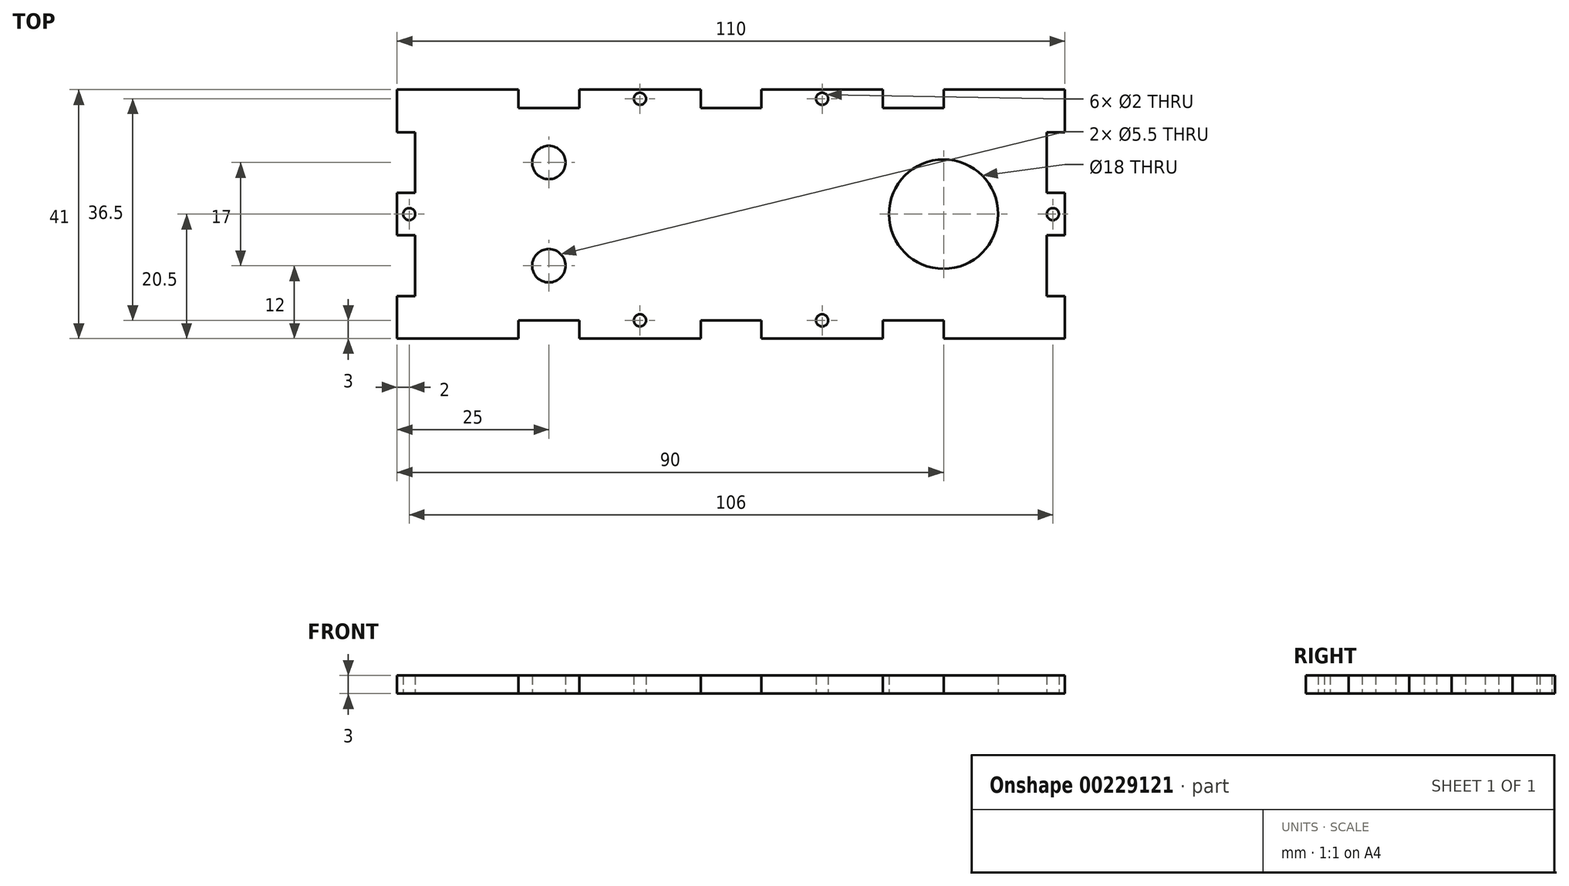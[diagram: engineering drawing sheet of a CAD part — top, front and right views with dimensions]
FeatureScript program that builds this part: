
annotation { "Feature Type Name" : "Feature", "Feature Type Description" : "" }
export const myFeature = defineFeature(function(context is Context, id is Id, definition is map)
    precondition{}
    {
        {
            var Q0;
            Q0=qCreatedBy(makeId("Top.planeOp"),FACE);
            var sketch = newSketch(context, id + "F0", { "sketchPlane" : qUnion([Q0])});
            skLineSegment(sketch, "E0", {"start": v(0, 0) * mm, "end": v(0, 7) * mm});
            skLineSegment(sketch, "E1", {"start": v(0, 7) * mm, "end": v(3, 7) * mm});
            skLineSegment(sketch, "E2", {"start": v(3, 7) * mm, "end": v(3, 17) * mm});
            skLineSegment(sketch, "E3", {"start": v(3, 17) * mm, "end": v(0, 17) * mm});
            skLineSegment(sketch, "E4", {"start": v(0, 17) * mm, "end": v(0, 24) * mm});
            skLineSegment(sketch, "E5", {"start": v(0, 24) * mm, "end": v(3, 24) * mm});
            skLineSegment(sketch, "E6", {"start": v(3, 24) * mm, "end": v(3, 34) * mm});
            skLineSegment(sketch, "E7", {"start": v(3, 34) * mm, "end": v(0, 34) * mm});
            skLineSegment(sketch, "E8", {"start": v(0, 34) * mm, "end": v(0, 41) * mm});
            skLineSegment(sketch, "E9", {"start": v(0, 0) * mm, "end": v(20, 0) * mm});
            skLineSegment(sketch, "E10", {"start": v(20, 0) * mm, "end": v(20, 3) * mm});
            skLineSegment(sketch, "E11", {"start": v(20, 3) * mm, "end": v(30, 3) * mm});
            skLineSegment(sketch, "E12", {"start": v(30, 3) * mm, "end": v(30, 0) * mm});
            skLineSegment(sketch, "E13", {"start": v(30, 0) * mm, "end": v(50, 0) * mm});
            skLineSegment(sketch, "E14", {"start": v(50, 0) * mm, "end": v(50, 3) * mm});
            skLineSegment(sketch, "E15", {"start": v(50, 3) * mm, "end": v(55, 3) * mm});
            skLineSegment(sketch, "E16", {"start": v(0, 20.5) * mm, "end": v(55, 20.5) * mm, "construction": true});
            skLineSegment(sketch, "E17.MirrorCS", {"start": v(30, 38) * mm, "end": v(30, 41) * mm});
            skLineSegment(sketch, "E18.MirrorCS", {"start": v(20, 38) * mm, "end": v(30, 38) * mm});
            skLineSegment(sketch, "E19.MirrorCS", {"start": v(20, 41) * mm, "end": v(20, 38) * mm});
            skLineSegment(sketch, "E20.MirrorCS", {"start": v(50, 38) * mm, "end": v(55, 38) * mm});
            skLineSegment(sketch, "E21.MirrorCS", {"start": v(0, 41) * mm, "end": v(20, 41) * mm});
            skLineSegment(sketch, "E22.MirrorCS", {"start": v(50, 41) * mm, "end": v(50, 38) * mm});
            skLineSegment(sketch, "E23.MirrorCS", {"start": v(30, 41) * mm, "end": v(50, 41) * mm});
            skLineSegment(sketch, "E24", {"start": v(55, 38) * mm, "end": v(55, 3) * mm, "construction": true});
            skCircle(sketch, "E25", {"center": v(2, 20.5) * mm, "radius": 1 * mm});
            skPoint(sketch, "E26.centerSnap0", {"position": v(40, 41) * mm});
            skPoint(sketch, "E26.centerSnap1", {"position": v(50, 39.5) * mm});
            skCircle(sketch, "E27", {"center": v(40, 39.5) * mm, "radius": 1 * mm});
            skLineSegment(sketch, "E28.MirrorCS", {"start": v(90, 0) * mm, "end": v(90, 3) * mm});
            skLineSegment(sketch, "E29.MirrorCS", {"start": v(80, 38) * mm, "end": v(80, 41) * mm});
            skLineSegment(sketch, "E30.MirrorCS", {"start": v(90, 41) * mm, "end": v(90, 38) * mm});
            skLineSegment(sketch, "E31.MirrorCS", {"start": v(110, 24) * mm, "end": v(107, 24) * mm});
            skLineSegment(sketch, "E32.MirrorCS", {"start": v(110, 7) * mm, "end": v(107, 7) * mm});
            skLineSegment(sketch, "E33.MirrorCS", {"start": v(107, 34) * mm, "end": v(110, 34) * mm});
            skLineSegment(sketch, "E34.MirrorCS", {"start": v(107, 17) * mm, "end": v(110, 17) * mm});
            skLineSegment(sketch, "E35.MirrorCS", {"start": v(60, 41) * mm, "end": v(60, 38) * mm});
            skLineSegment(sketch, "E36.MirrorCS", {"start": v(80, 3) * mm, "end": v(80, 0) * mm});
            skLineSegment(sketch, "E37.MirrorCS", {"start": v(60, 0) * mm, "end": v(60, 3) * mm});
            skCircle(sketch, "E38.MirrorC", {"center": v(70, 39.5) * mm, "radius": 1 * mm});
            skCircle(sketch, "E39.MirrorC", {"center": v(108, 20.5) * mm, "radius": 1 * mm});
            skLineSegment(sketch, "E40.MirrorCS", {"start": v(110, 34) * mm, "end": v(110, 41) * mm});
            skLineSegment(sketch, "E41.MirrorCS", {"start": v(110, 41) * mm, "end": v(90, 41) * mm});
            skLineSegment(sketch, "E42.MirrorCS", {"start": v(110, 0) * mm, "end": v(90, 0) * mm});
            skLineSegment(sketch, "E43.MirrorCS", {"start": v(90, 3) * mm, "end": v(80, 3) * mm});
            skPoint(sketch, "E44.MirrorP", {"position": v(60, 39.5) * mm});
            skLineSegment(sketch, "E45.MirrorCS", {"start": v(107, 7) * mm, "end": v(107, 17) * mm});
            skLineSegment(sketch, "E46.MirrorCS", {"start": v(90, 38) * mm, "end": v(80, 38) * mm});
            skLineSegment(sketch, "E47.MirrorCS", {"start": v(80, 41) * mm, "end": v(60, 41) * mm});
            skLineSegment(sketch, "E48.MirrorCS", {"start": v(110, 0) * mm, "end": v(110, 7) * mm});
            skLineSegment(sketch, "E49.MirrorCS", {"start": v(110, 17) * mm, "end": v(110, 24) * mm});
            skLineSegment(sketch, "E50.MirrorCS", {"start": v(60, 3) * mm, "end": v(55, 3) * mm});
            skLineSegment(sketch, "E51.MirrorCS", {"start": v(80, 0) * mm, "end": v(60, 0) * mm});
            skPoint(sketch, "E52.MirrorP", {"position": v(70, 41) * mm});
            skLineSegment(sketch, "E53.MirrorCS", {"start": v(60, 38) * mm, "end": v(55, 38) * mm});
            skLineSegment(sketch, "E54.MirrorCS", {"start": v(107, 24) * mm, "end": v(107, 34) * mm});
            skLineSegment(sketch, "E55.MirrorCS", {"start": v(110, 20.5) * mm, "end": v(55, 20.5) * mm, "construction": true});
            skCircle(sketch, "E56", {"center": v(90, 20.5) * mm, "radius": 9 * mm});
            skCircle(sketch, "E57", {"center": v(25, 29) * mm, "radius": 2.75 * mm});
            skPoint(sketch, "E57.centerSnap0", {"position": v(3, 29) * mm});
            skPoint(sketch, "E57.centerSnap1", {"position": v(25, 3) * mm});
            skCircle(sketch, "E58", {"center": v(25, 12) * mm, "radius": 2.75 * mm});
            skPoint(sketch, "E58.centerSnap0", {"position": v(3, 12) * mm});
            skPoint(sketch, "E58.centerSnap1", {"position": v(25, 38) * mm});
            skCircle(sketch, "E59", {"center": v(40, 3) * mm, "radius": 1 * mm});
            skPoint(sketch, "E59.centerSnap0", {"position": v(40, 0) * mm});
            skCircle(sketch, "E60", {"center": v(70, 3) * mm, "radius": 1 * mm});
            skPoint(sketch, "E60.centerSnap0", {"position": v(70, 0) * mm});
            skSolve(sketch);
        }
        {
            var Q0;
            Q0 = qSketchRegion(id + "F0", true);
            extrude(context, id + "F1", {"entities" : qUnion([Q0]), "depth" : 3 * mm});
        }
    });
